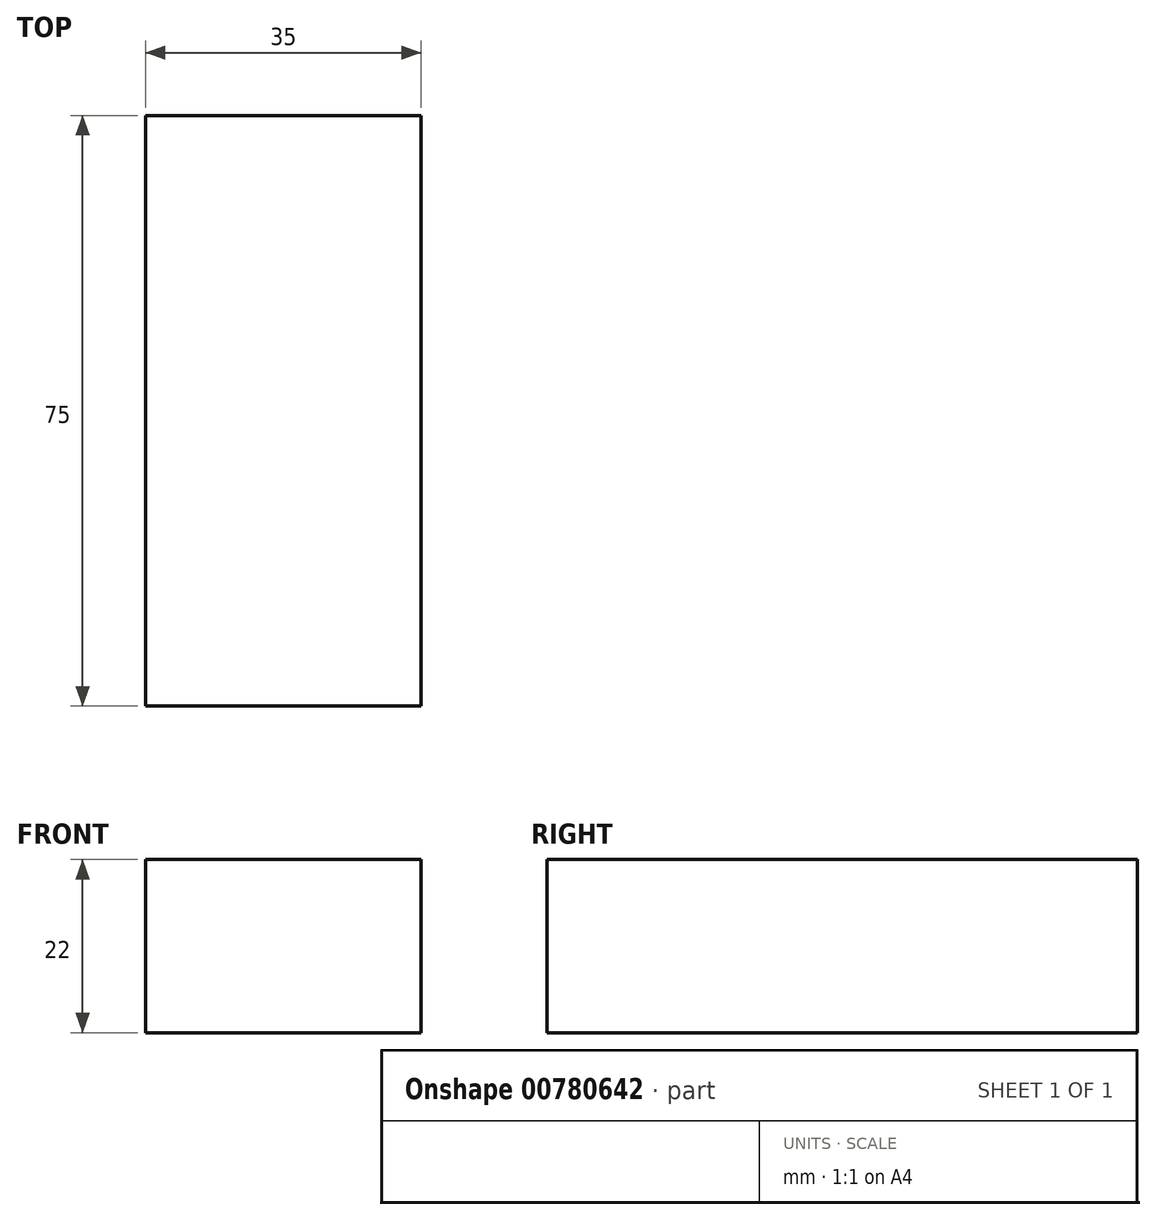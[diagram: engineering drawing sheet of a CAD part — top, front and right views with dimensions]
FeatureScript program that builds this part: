
annotation { "Feature Type Name" : "Feature", "Feature Type Description" : "" }
export const myFeature = defineFeature(function(context is Context, id is Id, definition is map)
    precondition{}
    {
        {
            var Q0;
            Q0=qCreatedBy(makeId("Top.planeOp"),FACE);
            var sketch = newSketch(context, id + "F0", { "sketchPlane" : qUnion([Q0])});
            skLineSegment(sketch, "E0.bottom", {"start": v(17.5, -37.5) * mm, "end": v(-17.5, -37.5) * mm});
            skLineSegment(sketch, "E0.top", {"start": v(17.5, 37.5) * mm, "end": v(-17.5, 37.5) * mm});
            skLineSegment(sketch, "E0.left", {"start": v(17.5, -37.5) * mm, "end": v(17.5, 37.5) * mm});
            skLineSegment(sketch, "E0.right", {"start": v(-17.5, -37.5) * mm, "end": v(-17.5, 37.5) * mm});
            skPoint(sketch, "E0.middle", {"position": v(0, 0) * mm});
            skSolve(sketch);
        }
        {
            var Q0;
            Q0=makeQuery(id+"F0.imprint","IMPRINT",FACE,{"disambiguationData":[TD([[makeQuery(id+"F0.imprint","IMPRINT",EDGE,{"derivedFrom":sQuery(id+"F0.wireOp",EDGE,"E0.bottom")}),-1.0]])]});
            extrude(context, id + "F1", {"entities" : qUnion([Q0]), "depth" : 22 * mm, "offsetDistance" : 25.4 * mm});
        }
    });
